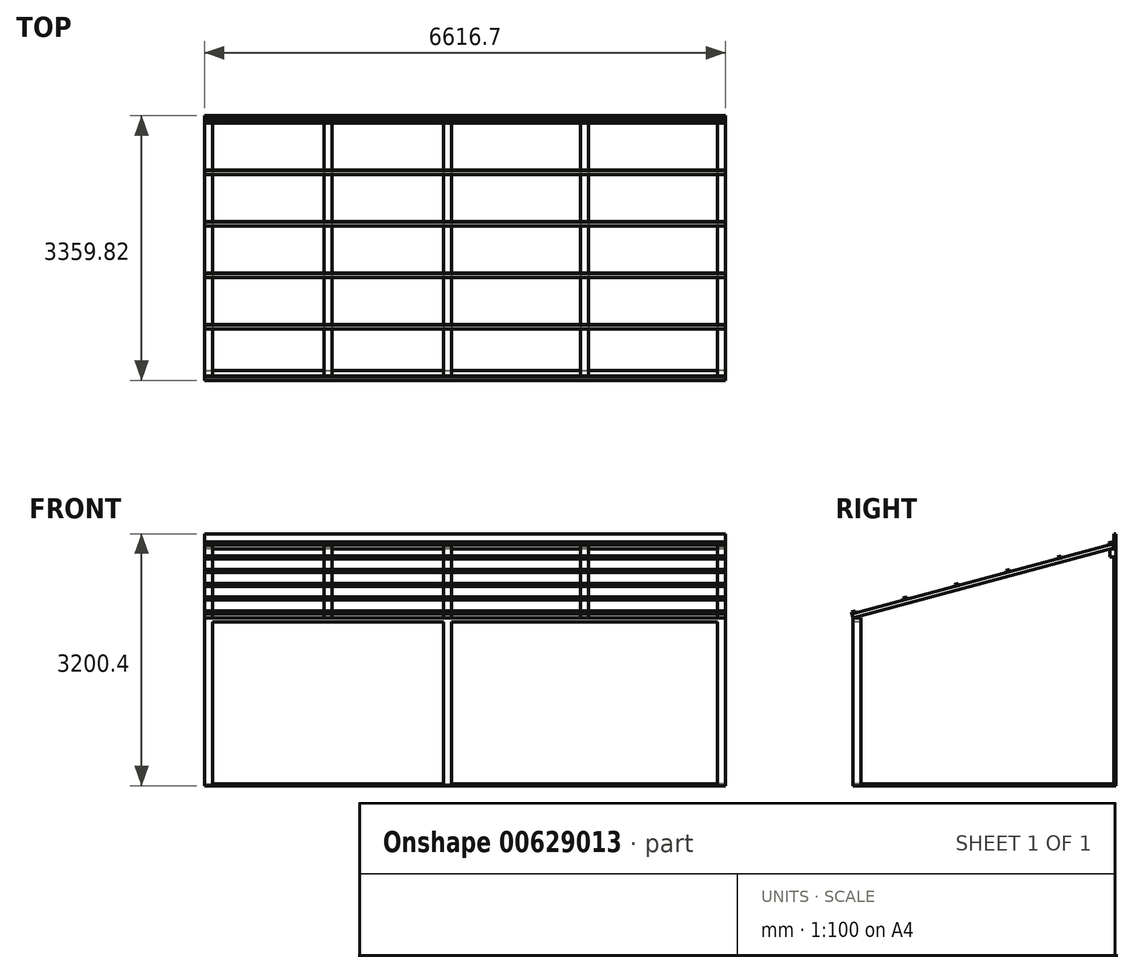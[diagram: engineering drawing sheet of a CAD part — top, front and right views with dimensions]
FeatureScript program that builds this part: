
annotation { "Feature Type Name" : "Feature", "Feature Type Description" : "" }
export const myFeature = defineFeature(function(context is Context, id is Id, definition is map)
    precondition{}
    {
        {
            var Q0;
            Q0=qCreatedBy(makeId("Top.planeOp"),FACE);
            var sketch = newSketch(context, id + "F0", { "sketchPlane" : qUnion([Q0])});
            skLineSegment(sketch, "E0.bottom", {"start": v(0, 0) * mm, "end": v(-6616.7, 0) * mm});
            skLineSegment(sketch, "E0.top", {"start": v(0, -3340.1) * mm, "end": v(-6616.7, -3340.1) * mm});
            skLineSegment(sketch, "E0.left", {"start": v(0, 0) * mm, "end": v(0, -3340.1) * mm});
            skLineSegment(sketch, "E0.right", {"start": v(-6616.7, 0) * mm, "end": v(-6616.7, -3340.1) * mm});
            skSolve(sketch);
        }
        {
            var Q0;
            Q0=makeQuery(id+"F0.imprint","IMPRINT",FACE,{"disambiguationData":[TD([[makeQuery(id+"F0.imprint","IMPRINT",EDGE,{"derivedFrom":sQuery(id+"F0.wireOp",EDGE,"E0.bottom")}),1.0]])]});
            extrude(context, id + "F1", {"entities" : qUnion([Q0]), "depth" : 25.4 * mm, "offsetDistance" : 25.4 * mm});
        }
        {
            var Q0;
            Q0=makeQuery(id+"F1.opExtrude","CAP_FACE",FACE,{"disambiguationData":[OSD([sQuery(id+"F0.wireOp",EDGE,"E0.bottom"),sQuery(id+"F0.wireOp",EDGE,"E0.top"),sQuery(id+"F0.wireOp",EDGE,"E0.left"),sQuery(id+"F0.wireOp",EDGE,"E0.right")])],"isStart":false});
            var sketch = newSketch(context, id + "F2", { "sketchPlane" : qUnion([Q0])});
            skLineSegment(sketch, "E1", {"start": v(-6616.7, -25.4) * mm, "end": v(0, -25.4) * mm});
            skSolve(sketch);
        }
        {
            var Q0;
            {var subQ0=sQuery(id+"F2.wireOp",EDGE,"E1");Q0=makeQuery(id+"F2.imprint","IMPRINT",FACE,{"disambiguationData":[TD([[makeQuery(id+"F2.imprint","IMPRINT",EDGE,{"derivedFrom":subQ0}),1.0]])]});}
            extrude(context, id + "F3", {"entities" : qUnion([Q0]), "operationType" : NewBodyOperationType.ADD, "depth" : 3175 * mm, "offsetDistance" : 25.4 * mm});
        }
        {
            var Q0;
            Q0=makeQuery(id+"F1.opExtrude","CAP_FACE",FACE,{"disambiguationData":[OSD([sQuery(id+"F0.wireOp",EDGE,"E0.bottom"),sQuery(id+"F0.wireOp",EDGE,"E0.top"),sQuery(id+"F0.wireOp",EDGE,"E0.left"),sQuery(id+"F0.wireOp",EDGE,"E0.right")])],"isStart":false});
            var sketch = newSketch(context, id + "F4", { "sketchPlane" : qUnion([Q0])});
            skLineSegment(sketch, "E2.bottom", {"start": v(-6616.7, -3238.5) * mm, "end": v(-6515.1, -3238.5) * mm});
            skLineSegment(sketch, "E2.top", {"start": v(-6616.7, -3340.1) * mm, "end": v(-6515.1, -3340.1) * mm});
            skLineSegment(sketch, "E2.left", {"start": v(-6616.7, -3238.5) * mm, "end": v(-6616.7, -3340.1) * mm});
            skLineSegment(sketch, "E2.right", {"start": v(-6515.1, -3238.5) * mm, "end": v(-6515.1, -3340.1) * mm});
            skLineSegment(sketch, "E3.bottom", {"start": v(0, -3238.5) * mm, "end": v(-101.6, -3238.5) * mm});
            skLineSegment(sketch, "E3.top", {"start": v(0, -3340.1) * mm, "end": v(-101.6, -3340.1) * mm});
            skLineSegment(sketch, "E3.left", {"start": v(0, -3238.5) * mm, "end": v(0, -3340.1) * mm});
            skLineSegment(sketch, "E3.right", {"start": v(-101.6, -3238.5) * mm, "end": v(-101.6, -3340.1) * mm});
            skLineSegment(sketch, "E4.bottom", {"start": v(-3581.4, -3238.5) * mm, "end": v(-3479.8, -3238.5) * mm});
            skLineSegment(sketch, "E4.top", {"start": v(-3581.4, -3340.1) * mm, "end": v(-3479.8, -3340.1) * mm});
            skLineSegment(sketch, "E4.left", {"start": v(-3581.4, -3238.5) * mm, "end": v(-3581.4, -3340.1) * mm});
            skLineSegment(sketch, "E4.right", {"start": v(-3479.8, -3238.5) * mm, "end": v(-3479.8, -3340.1) * mm});
            skSolve(sketch);
        }
        {
            var Q0;
            Q0=makeQuery(id+"F4.imprint","IMPRINT",FACE,{"disambiguationData":[TD([[makeQuery(id+"F4.imprint","IMPRINT",EDGE,{"derivedFrom":sQuery(id+"F4.wireOp",EDGE,"E2.bottom")}),-1.0]])]});
            var Q1;
            Q1=makeQuery(id+"F4.imprint","IMPRINT",FACE,{"disambiguationData":[TD([[makeQuery(id+"F4.imprint","IMPRINT",EDGE,{"derivedFrom":sQuery(id+"F4.wireOp",EDGE,"E4.bottom")}),-1.0]])]});
            var Q2;
            Q2=makeQuery(id+"F4.imprint","IMPRINT",FACE,{"disambiguationData":[TD([[makeQuery(id+"F4.imprint","IMPRINT",EDGE,{"derivedFrom":sQuery(id+"F4.wireOp",EDGE,"E3.bottom")}),1.0]])]});
            extrude(context, id + "F5", {"entities" : qUnion([Q0, Q1, Q2]), "operationType" : NewBodyOperationType.ADD, "depth" : 2057.4 * mm, "offsetDistance" : 25.4 * mm});
        }
        {
            var Q0;
            Q0=makeQuery(id+"F5.opExtrude","CAP_FACE",FACE,{"disambiguationData":[OSD([sQuery(id+"F4.wireOp",EDGE,"E2.bottom"),sQuery(id+"F4.wireOp",EDGE,"E2.top"),sQuery(id+"F4.wireOp",EDGE,"E2.left"),sQuery(id+"F4.wireOp",EDGE,"E2.right")])],"isStart":false});
            var sketch = newSketch(context, id + "F6", { "sketchPlane" : qUnion([Q0])});
            skLineSegment(sketch, "E5.bottom", {"start": v(-6616.7, -3340.1) * mm, "end": v(0, -3340.1) * mm});
            skLineSegment(sketch, "E5.top", {"start": v(-6616.7, -3238.5) * mm, "end": v(0, -3238.5) * mm});
            skLineSegment(sketch, "E5.left", {"start": v(-6616.7, -3340.1) * mm, "end": v(-6616.7, -3238.5) * mm});
            skLineSegment(sketch, "E5.right", {"start": v(0, -3340.1) * mm, "end": v(0, -3238.5) * mm});
            skSolve(sketch);
        }
        {
            var Q0;
            {var subQ0=sQuery(id+"F6.wireOp",EDGE,"E5.left");Q0=makeQuery(id+"F6.imprint","IMPRINT",FACE,{"disambiguationData":[TD([[makeQuery(id+"F6.imprint","IMPRINT",EDGE,{"derivedFrom":subQ0}),1.0]])]});}
            var Q1;
            {var subQ2=sQuery(id+"F6.wireOp",EDGE,"E5.right");Q1=makeQuery(id+"F6.imprint","IMPRINT",FACE,{"disambiguationData":[TD([[makeQuery(id+"F6.imprint","IMPRINT",EDGE,{"derivedFrom":subQ2}),1.0]])]});}
            extrude(context, id + "F7", {"entities" : qUnion([Q0, Q1]), "operationType" : NewBodyOperationType.ADD, "depth" : 50.8 * mm, "offsetDistance" : 25.4 * mm});
        }
        {
            var Q0;
            {var subQ0=sQuery(id+"F0.wireOp",EDGE,"E0.right");Q0=makeQuery(id+"F7.boolean.opBoolean","MERGE",FACE,{"derivedFrom":[makeQuery(id+"F5.boolean.opBoolean","MERGE",FACE,{"derivedFrom":[makeQuery(id+"F3.boolean.opBoolean","MERGE",FACE,{"derivedFrom":[makeQuery(id+"F1.opExtrude","SWEPT_FACE",FACE,{"disambiguationData":[OSD([subQ0])]}),makeQuery(id+"F3.opExtrude","SWEPT_FACE",FACE,{"disambiguationData":[OSD([subQ0])]})]}),makeQuery(id+"F5.opExtrude","SWEPT_FACE",FACE,{"disambiguationData":[OSD([sQuery(id+"F4.wireOp",EDGE,"E2.left")])]})]}),makeQuery(id+"F7.opExtrude","SWEPT_FACE",FACE,{"disambiguationData":[OSD([sQuery(id+"F6.wireOp",EDGE,"E5.left")])]})]});}
            var sketch = newSketch(context, id + "F8", { "sketchPlane" : qUnion([Q0])});
            skLineSegment(sketch, "E6", {"start": v(25.4, 2906.56) * mm, "end": v(76.2, 2906.56) * mm});
            skLineSegment(sketch, "E7", {"start": v(76.2, 2906.56) * mm, "end": v(76.2, 3008.16) * mm});
            skLineSegment(sketch, "E8", {"start": v(76.2, 3008.16) * mm, "end": v(25.4, 3008.16) * mm});
            skLineSegment(sketch, "E9", {"start": v(76.2, 3008.16) * mm, "end": v(3340.1, 2133.6) * mm});
            skLineSegment(sketch, "E10", {"start": v(3340.1, 2133.6) * mm, "end": v(3353.25, 2182.67) * mm});
            skLineSegment(sketch, "E11", {"start": v(76.2, 3008.16) * mm, "end": v(25.4, 3021.77) * mm});
            skLineSegment(sketch, "E12", {"start": v(25.4, 3021.77) * mm, "end": v(38.55, 3070.84) * mm});
            skLineSegment(sketch, "E13", {"start": v(38.55, 3070.84) * mm, "end": v(3353.25, 2182.67) * mm});
            skSolve(sketch);
        }
        {
            var Q0;
            {var subQ0=sQuery(id+"F8.wireOp",EDGE,"E6");Q0=makeQuery(id+"F8.imprint","IMPRINT",FACE,{"disambiguationData":[TD([[makeQuery(id+"F8.imprint","IMPRINT",EDGE,{"derivedFrom":subQ0}),1.0]])]});}
            var Q1;
            Q1=makeQuery(id+"F8.imprint","IMPRINT",FACE,{"disambiguationData":[TD([[makeQuery(id+"F8.imprint","IMPRINT",EDGE,{"derivedFrom":sQuery(id+"F8.wireOp",EDGE,"E9")}),1.0]])]});
            extrude(context, id + "F9", {"entities" : qUnion([Q0, Q1]), "operationType" : NewBodyOperationType.ADD, "oppositeDirection" : true, "depth" : 6616.7 * mm, "offsetDistance" : 25.4 * mm});
        }
        {
            var Q0;
            Q0=makeQuery(id+"F9.opExtrude","SWEPT_FACE",FACE,{"disambiguationData":[OSD([sQuery(id+"F8.wireOp",EDGE,"E13")])]});
            var sketch = newSketch(context, id + "F10", { "sketchPlane" : qUnion([Q0])});
            skLineSegment(sketch, "E14", {"start": v(-6515.1, 757.56) * mm, "end": v(-6515.1, -2674.07) * mm});
            skLineSegment(sketch, "E15", {"start": v(-101.6, 757.56) * mm, "end": v(-101.6, -2674.07) * mm});
            skLineSegment(sketch, "E16.bottom", {"start": v(-3581.4, 757.56) * mm, "end": v(-3479.8, 757.56) * mm});
            skLineSegment(sketch, "E16.top", {"start": v(-3581.4, -2674.07) * mm, "end": v(-3479.8, -2674.07) * mm});
            skLineSegment(sketch, "E16.left", {"start": v(-3581.4, 757.56) * mm, "end": v(-3581.4, -2674.07) * mm});
            skLineSegment(sketch, "E16.right", {"start": v(-3479.8, 757.56) * mm, "end": v(-3479.8, -2674.07) * mm});
            skLineSegment(sketch, "E17.bottom", {"start": v(-5099.05, 757.56) * mm, "end": v(-4997.45, 757.56) * mm});
            skLineSegment(sketch, "E17.top", {"start": v(-5099.05, -2674.07) * mm, "end": v(-4997.45, -2674.07) * mm});
            skLineSegment(sketch, "E17.left", {"start": v(-5099.05, 757.56) * mm, "end": v(-5099.05, -2674.07) * mm});
            skLineSegment(sketch, "E17.right", {"start": v(-4997.45, 757.56) * mm, "end": v(-4997.45, -2674.07) * mm});
            skLineSegment(sketch, "E18.bottom", {"start": v(-1841.5, 757.56) * mm, "end": v(-1739.9, 757.56) * mm});
            skLineSegment(sketch, "E18.top", {"start": v(-1841.5, -2674.07) * mm, "end": v(-1739.9, -2674.07) * mm});
            skLineSegment(sketch, "E18.left", {"start": v(-1841.5, 757.56) * mm, "end": v(-1841.5, -2674.07) * mm});
            skLineSegment(sketch, "E18.right", {"start": v(-1739.9, 757.56) * mm, "end": v(-1739.9, -2674.07) * mm});
            skSolve(sketch);
        }
        {
            var Q0;
            {var subQ0=sQuery(id+"F10.wireOp",EDGE,"E14");Q0=makeQuery(id+"F10.imprint","IMPRINT",FACE,{"disambiguationData":[TD([[makeQuery(id+"F10.imprint","IMPRINT",EDGE,{"derivedFrom":subQ0}),1.0]])]});}
            var Q1;
            {var subQ0=sQuery(id+"F10.wireOp",EDGE,"E16.left");Q1=makeQuery(id+"F10.imprint","IMPRINT",FACE,{"disambiguationData":[TD([[makeQuery(id+"F10.imprint","IMPRINT",EDGE,{"derivedFrom":subQ0}),-1.0]])]});}
            var Q2;
            {var subQ0=sQuery(id+"F10.wireOp",EDGE,"E16.right");Q2=makeQuery(id+"F10.imprint","IMPRINT",FACE,{"disambiguationData":[TD([[makeQuery(id+"F10.imprint","IMPRINT",EDGE,{"derivedFrom":subQ0}),1.0]])]});}
            var Q3;
            {var subQ0=sQuery(id+"F10.wireOp",EDGE,"E15");Q3=makeQuery(id+"F10.imprint","IMPRINT",FACE,{"disambiguationData":[TD([[makeQuery(id+"F10.imprint","IMPRINT",EDGE,{"derivedFrom":subQ0}),-1.0]])]});}
            extrude(context, id + "F11", {"entities" : qUnion([Q0, Q1, Q2, Q3]), "operationType" : NewBodyOperationType.REMOVE, "oppositeDirection" : true, "depth" : 50.8 * mm, "offsetDistance" : 25.4 * mm});
        }
        {
            var Q0;
            {var subQ0=sQuery(id+"F8.wireOp",EDGE,"E13");Q0=makeQuery(id+"F11.boolean.opBoolean","SPLIT",FACE,{"disambiguationData":[TD([makeQuery(id+"F11.opExtrude","SWEPT_FACE",FACE,{"disambiguationData":[OSD([sQuery(id+"F10.wireOp",EDGE,"E14")])]})])],"derivedFrom":makeQuery(id+"F9.opExtrude","SWEPT_FACE",FACE,{"disambiguationData":[OSD([subQ0])]})});}
            var sketch = newSketch(context, id + "F12", { "sketchPlane" : qUnion([Q0])});
            skLineSegment(sketch, "E19.bottom", {"start": v(-6616.7, -594.74) * mm, "end": v(0, -594.74) * mm});
            skLineSegment(sketch, "E19.top", {"start": v(-6616.7, -645.54) * mm, "end": v(0, -645.54) * mm});
            skLineSegment(sketch, "E19.left", {"start": v(-6616.7, -594.74) * mm, "end": v(-6616.7, -645.54) * mm});
            skLineSegment(sketch, "E19.right", {"start": v(0, -594.74) * mm, "end": v(0, -645.54) * mm});
            skLineSegment(sketch, "E20.bottom", {"start": v(-6616.7, -1270.89) * mm, "end": v(0, -1270.89) * mm});
            skLineSegment(sketch, "E20.top", {"start": v(-6616.7, -1321.69) * mm, "end": v(0, -1321.69) * mm});
            skLineSegment(sketch, "E20.left", {"start": v(-6616.7, -1270.89) * mm, "end": v(-6616.7, -1321.69) * mm});
            skLineSegment(sketch, "E20.right", {"start": v(0, -1270.89) * mm, "end": v(0, -1321.69) * mm});
            skLineSegment(sketch, "E21.bottom", {"start": v(-6616.7, 81.4) * mm, "end": v(0, 81.4) * mm});
            skLineSegment(sketch, "E21.top", {"start": v(-6616.7, 30.6) * mm, "end": v(0, 30.6) * mm});
            skLineSegment(sketch, "E21.left", {"start": v(-6616.7, 81.4) * mm, "end": v(-6616.7, 30.6) * mm});
            skLineSegment(sketch, "E21.right", {"start": v(0, 81.4) * mm, "end": v(0, 30.6) * mm});
            skLineSegment(sketch, "E22.bottom", {"start": v(-6616.7, -1947.03) * mm, "end": v(0, -1947.03) * mm});
            skLineSegment(sketch, "E22.top", {"start": v(-6616.7, -1997.83) * mm, "end": v(0, -1997.83) * mm});
            skLineSegment(sketch, "E22.left", {"start": v(-6616.7, -1947.03) * mm, "end": v(-6616.7, -1997.83) * mm});
            skLineSegment(sketch, "E22.right", {"start": v(0, -1947.03) * mm, "end": v(0, -1997.83) * mm});
            skLineSegment(sketch, "E23.bottom", {"start": v(-6616.7, 757.56) * mm, "end": v(0, 757.56) * mm});
            skLineSegment(sketch, "E23.top", {"start": v(-6616.7, 706.76) * mm, "end": v(0, 706.76) * mm});
            skLineSegment(sketch, "E23.left", {"start": v(-6616.7, 757.56) * mm, "end": v(-6616.7, 706.76) * mm});
            skLineSegment(sketch, "E23.right", {"start": v(0, 757.56) * mm, "end": v(0, 706.76) * mm});
            skLineSegment(sketch, "E24.bottom", {"start": v(-6616.7, -2674.07) * mm, "end": v(0, -2674.07) * mm});
            skLineSegment(sketch, "E24.top", {"start": v(-6616.7, -2623.27) * mm, "end": v(0, -2623.27) * mm});
            skLineSegment(sketch, "E24.left", {"start": v(-6616.7, -2674.07) * mm, "end": v(-6616.7, -2623.27) * mm});
            skLineSegment(sketch, "E24.right", {"start": v(0, -2674.07) * mm, "end": v(0, -2623.27) * mm});
            skSolve(sketch);
        }
        {
            var Q0;
            {var subQ0=sQuery(id+"F12.wireOp",EDGE,"E23.left");Q0=makeQuery(id+"F12.imprint","IMPRINT",FACE,{"disambiguationData":[TD([[makeQuery(id+"F12.imprint","IMPRINT",EDGE,{"derivedFrom":subQ0}),1.0]])]});}
            var Q1;
            {var subQ3=sQuery(id+"F12.wireOp",EDGE,"E23.right");Q1=makeQuery(id+"F12.imprint","IMPRINT",FACE,{"disambiguationData":[TD([[makeQuery(id+"F12.imprint","IMPRINT",EDGE,{"derivedFrom":subQ3}),-1.0]])]});}
            var Q2;
            {var subQ0=sQuery(id+"F12.wireOp",EDGE,"E21.left");Q2=makeQuery(id+"F12.imprint","IMPRINT",FACE,{"disambiguationData":[TD([[makeQuery(id+"F12.imprint","IMPRINT",EDGE,{"derivedFrom":subQ0}),1.0]])]});}
            var Q3;
            {var subQ0=sQuery(id+"F12.wireOp",EDGE,"E21.right");Q3=makeQuery(id+"F12.imprint","IMPRINT",FACE,{"disambiguationData":[TD([[makeQuery(id+"F12.imprint","IMPRINT",EDGE,{"derivedFrom":subQ0}),-1.0]])]});}
            var Q4;
            {var subQ0=sQuery(id+"F12.wireOp",EDGE,"E19.left");Q4=makeQuery(id+"F12.imprint","IMPRINT",FACE,{"disambiguationData":[TD([[makeQuery(id+"F12.imprint","IMPRINT",EDGE,{"derivedFrom":subQ0}),1.0]])]});}
            var Q5;
            {var subQ0=sQuery(id+"F12.wireOp",EDGE,"E19.right");Q5=makeQuery(id+"F12.imprint","IMPRINT",FACE,{"disambiguationData":[TD([[makeQuery(id+"F12.imprint","IMPRINT",EDGE,{"derivedFrom":subQ0}),-1.0]])]});}
            var Q6;
            {var subQ0=sQuery(id+"F12.wireOp",EDGE,"E24.left");Q6=makeQuery(id+"F12.imprint","IMPRINT",FACE,{"disambiguationData":[TD([[makeQuery(id+"F12.imprint","IMPRINT",EDGE,{"derivedFrom":subQ0}),1.0]])]});}
            var Q7;
            {var subQ3=sQuery(id+"F12.wireOp",EDGE,"E24.right");Q7=makeQuery(id+"F12.imprint","IMPRINT",FACE,{"disambiguationData":[TD([[makeQuery(id+"F12.imprint","IMPRINT",EDGE,{"derivedFrom":subQ3}),1.0]])]});}
            var Q8;
            {var subQ0=sQuery(id+"F12.wireOp",EDGE,"E22.left");Q8=makeQuery(id+"F12.imprint","IMPRINT",FACE,{"disambiguationData":[TD([[makeQuery(id+"F12.imprint","IMPRINT",EDGE,{"derivedFrom":subQ0}),1.0]])]});}
            var Q9;
            {var subQ0=sQuery(id+"F12.wireOp",EDGE,"E22.right");Q9=makeQuery(id+"F12.imprint","IMPRINT",FACE,{"disambiguationData":[TD([[makeQuery(id+"F12.imprint","IMPRINT",EDGE,{"derivedFrom":subQ0}),-1.0]])]});}
            var Q10;
            {var subQ0=sQuery(id+"F12.wireOp",EDGE,"E20.left");Q10=makeQuery(id+"F12.imprint","IMPRINT",FACE,{"disambiguationData":[TD([[makeQuery(id+"F12.imprint","IMPRINT",EDGE,{"derivedFrom":subQ0}),1.0]])]});}
            var Q11;
            {var subQ0=sQuery(id+"F12.wireOp",EDGE,"E20.right");Q11=makeQuery(id+"F12.imprint","IMPRINT",FACE,{"disambiguationData":[TD([[makeQuery(id+"F12.imprint","IMPRINT",EDGE,{"derivedFrom":subQ0}),-1.0]])]});}
            extrude(context, id + "F13", {"entities" : qUnion([Q0, Q1, Q2, Q3, Q4, Q5, Q6, Q7, Q8, Q9, Q10, Q11]), "depth" : 25.4 * mm, "offsetDistance" : 25.4 * mm});
        }
    });
